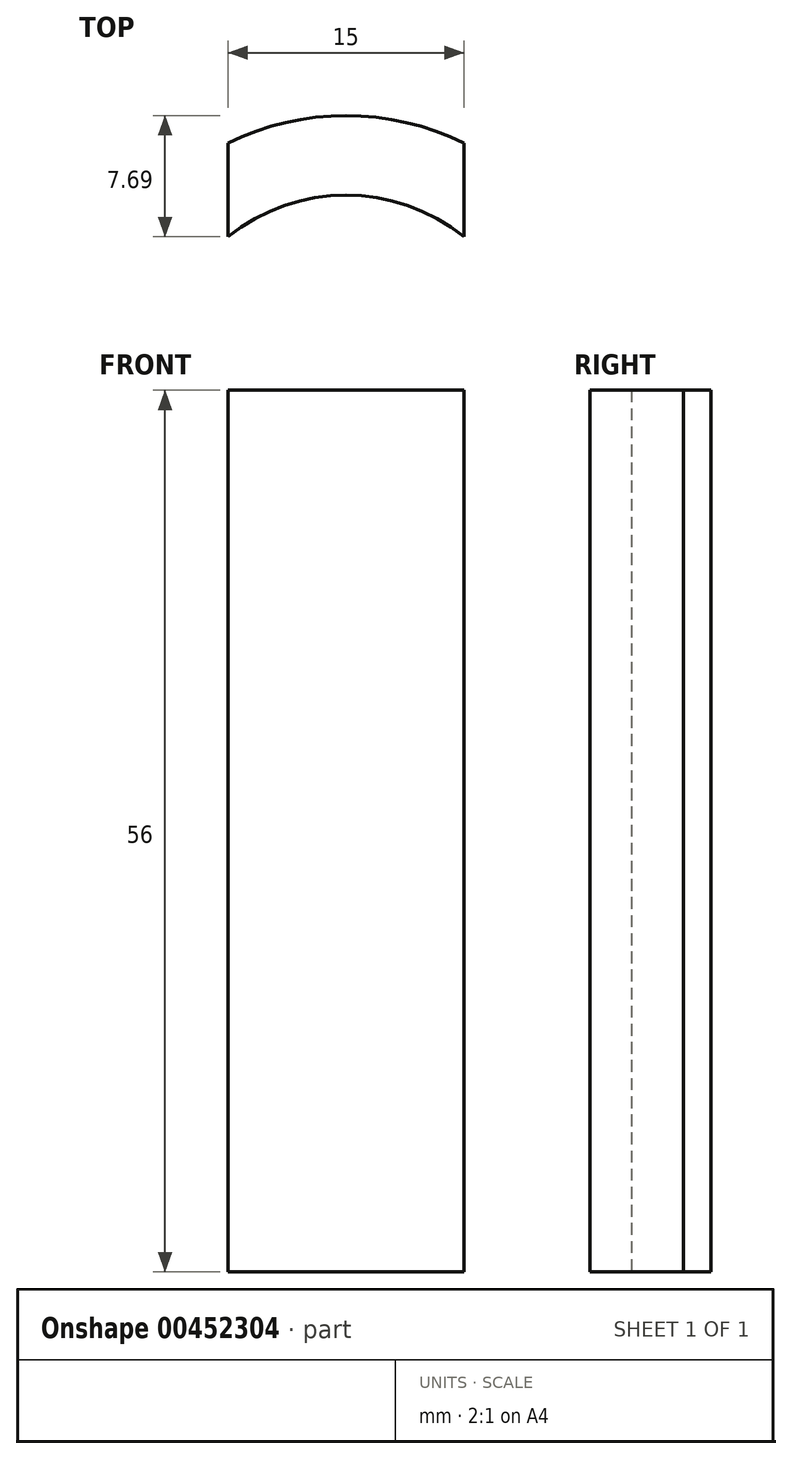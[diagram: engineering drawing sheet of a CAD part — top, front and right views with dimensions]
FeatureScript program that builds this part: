
annotation { "Feature Type Name" : "Feature", "Feature Type Description" : "" }
export const myFeature = defineFeature(function(context is Context, id is Id, definition is map)
    precondition{}
    {
        {
            var Q0;
            Q0=qCreatedBy(makeId("Top.planeOp"),FACE);
            var sketch = newSketch(context, id + "F0", { "sketchPlane" : qUnion([Q0])});
            skArc(sketch, "E0", {"start": v(7.5, 15.29) * mm, "mid": v(0, 17.03) * mm, "end": v(-7.5, 15.29) * mm});
            skArc(sketch, "E1", {"start": v(7.5, 9.34) * mm, "mid": v(0, 11.98) * mm, "end": v(-7.5, 9.34) * mm});
            skLineSegment(sketch, "E2.left", {"start": v(7.5, 9.34) * mm, "end": v(7.5, 15.29) * mm});
            skLineSegment(sketch, "E2.right", {"start": v(-7.5, 9.34) * mm, "end": v(-7.5, 15.29) * mm});
            skPoint(sketch, "E2.middle", {"position": v(0, 17.03) * mm});
            skPoint(sketch, "E3.orphan", {"position": v(-7.5, 28.3) * mm});
            skPoint(sketch, "E4.orphan", {"position": v(7.5, 28.3) * mm});
            skPoint(sketch, "E5.orphan", {"position": v(7.5, 5.75) * mm});
            skPoint(sketch, "E6.orphan", {"position": v(-7.5, 5.75) * mm});
            skSolve(sketch);
        }
        {
            var Q0;
            Q0 = qSketchRegion(id + "F0", true);
            extrude(context, id + "F1", {"entities" : qUnion([Q0]), "depth" : 56 * mm});
        }
    });
